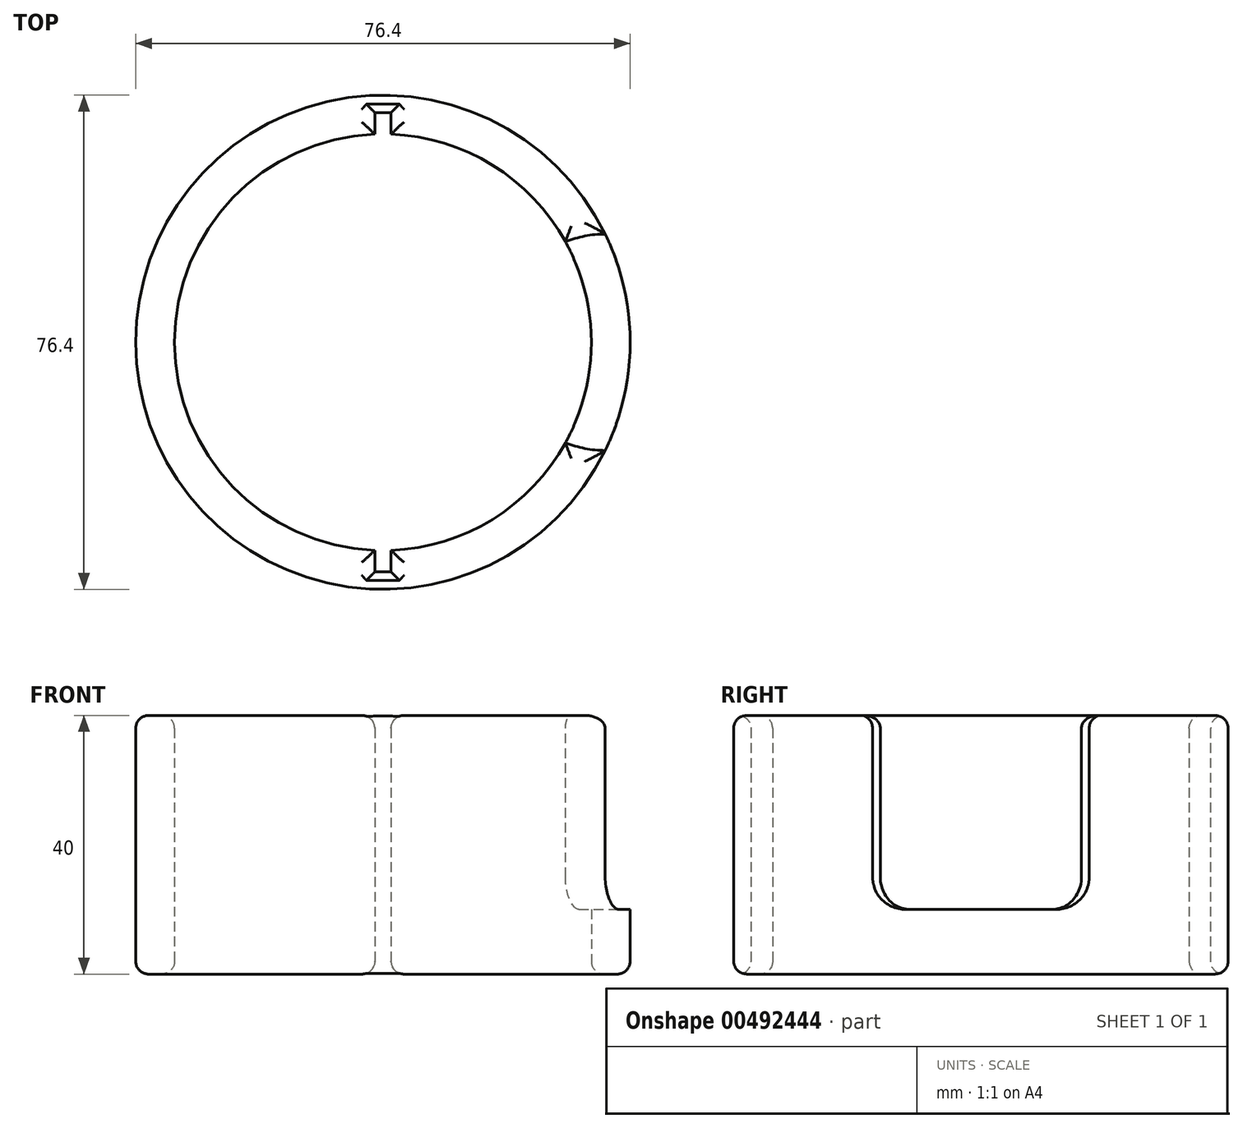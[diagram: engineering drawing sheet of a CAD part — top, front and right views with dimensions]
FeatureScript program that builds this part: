
annotation { "Feature Type Name" : "Feature", "Feature Type Description" : "" }
export const myFeature = defineFeature(function(context is Context, id is Id, definition is map)
    precondition{}
    {
        {
            var Q0;
            Q0=qCreatedBy(makeId("Top.planeOp"),FACE);
            var sketch = newSketch(context, id + "F0", { "sketchPlane" : qUnion([Q0])});
            skCircle(sketch, "E0", {"center": v(0, 0) * mm, "radius": 32.2 * mm});
            skCircle(sketch, "E1", {"center": v(0, 0) * mm, "radius": 38.2 * mm});
            skSolve(sketch);
        }
        {
            var Q0;
            Q0=makeQuery(id+"F0.imprint","IMPRINT",FACE,{"disambiguationData":[TD([[makeQuery(id+"F0.imprint","IMPRINT",EDGE,{"derivedFrom":sQuery(id+"F0.wireOp",EDGE,"E0")}),-1.0]])]});
            extrude(context, id + "F1", {"entities" : qUnion([Q0]), "depth" : 40 * mm});
        }
        {
            var Q0;
            Q0=makeQuery(id+"F1.opExtrude","CAP_FACE",FACE,{"disambiguationData":[OSD([sQuery(id+"F0.wireOp",EDGE,"E0"),sQuery(id+"F0.wireOp",EDGE,"E1")])],"isStart":false});
            var sketch = newSketch(context, id + "F2", { "sketchPlane" : qUnion([Q0])});
            skLineSegment(sketch, "E2.bottom", {"start": v(-1.25, 35.5) * mm, "end": v(1.25, 35.5) * mm});
            skLineSegment(sketch, "E2.top", {"start": v(-1.25, 31.5) * mm, "end": v(1.25, 31.5) * mm});
            skLineSegment(sketch, "E2.left", {"start": v(-1.25, 35.5) * mm, "end": v(-1.25, 31.5) * mm});
            skLineSegment(sketch, "E2.right", {"start": v(1.25, 35.5) * mm, "end": v(1.25, 31.5) * mm});
            skLineSegment(sketch, "E3.bottom", {"start": v(-1.25, -35.5) * mm, "end": v(1.25, -35.5) * mm});
            skLineSegment(sketch, "E3.top", {"start": v(-1.25, -31.5) * mm, "end": v(1.25, -31.5) * mm});
            skLineSegment(sketch, "E3.left", {"start": v(-1.25, -31.5) * mm, "end": v(-1.25, -35.5) * mm});
            skLineSegment(sketch, "E3.right", {"start": v(1.25, -31.5) * mm, "end": v(1.25, -35.5) * mm});
            skSolve(sketch);
        }
        {
            var Q0;
            {var subQ0=sQuery(id+"F2.wireOp",EDGE,"E3.bottom");Q0=makeQuery(id+"F2.imprint","IMPRINT",FACE,{"disambiguationData":[TD([[makeQuery(id+"F2.imprint","IMPRINT",EDGE,{"derivedFrom":subQ0}),1.0]])]});}
            var Q1;
            {var subQ0=sQuery(id+"F2.wireOp",EDGE,"E3.top");Q1=makeQuery(id+"F2.imprint","IMPRINT",FACE,{"disambiguationData":[TD([[makeQuery(id+"F2.imprint","IMPRINT",EDGE,{"derivedFrom":subQ0}),-1.0]])]});}
            var Q2;
            {var subQ0=sQuery(id+"F2.wireOp",EDGE,"E2.top");Q2=makeQuery(id+"F2.imprint","IMPRINT",FACE,{"disambiguationData":[TD([[makeQuery(id+"F2.imprint","IMPRINT",EDGE,{"derivedFrom":subQ0}),1.0]])]});}
            var Q3;
            {var subQ0=sQuery(id+"F2.wireOp",EDGE,"E2.bottom");Q3=makeQuery(id+"F2.imprint","IMPRINT",FACE,{"disambiguationData":[TD([[makeQuery(id+"F2.imprint","IMPRINT",EDGE,{"derivedFrom":subQ0}),-1.0]])]});}
            extrude(context, id + "F3", {"entities" : qUnion([Q0, Q1, Q2, Q3]), "operationType" : NewBodyOperationType.REMOVE, "endBound" : BoundingType.THROUGH_ALL, "oppositeDirection" : true, "depth" : 25 * mm});
        }
        {
            var Q0;
            Q0=makeQuery(id+"F1.opExtrude","CAP_FACE",FACE,{"disambiguationData":[OSD([sQuery(id+"F0.wireOp",EDGE,"E0"),sQuery(id+"F0.wireOp",EDGE,"E1")])],"isStart":false});
            var sketch = newSketch(context, id + "F4", { "sketchPlane" : qUnion([Q0])});
            skCircle(sketch, "E4", {"center": v(34.42, 0) * mm, "radius": 16.73 * mm});
            skSolve(sketch);
        }
        {
            var Q0;
            {var subQ0=sQuery(id+"F4.wireOp",EDGE,"E4");var subQ1=sQuery(id+"F0.wireOp",EDGE,"E1");var subQ2=makeQuery(id+"F1.opExtrude","CAP_EDGE",EDGE,{"disambiguationData":[OSD([subQ1])],"isStart":false});var subQ3=makeQuery(id+"F4.imprint","INTERSECT",VERTEX,{"disambiguationData":[OD(0.0)],"derivedFrom":[subQ2,subQ0]});Q0=makeQuery(id+"F4.imprint","IMPRINT",FACE,{"disambiguationData":[TD([[makeQuery(id+"F4.imprint","IMPRINT",EDGE,{"disambiguationData":[TD([[subQ3,1.0]])],"derivedFrom":subQ2}),1.0]])]});}
            extrude(context, id + "F5", {"entities" : qUnion([Q0]), "operationType" : NewBodyOperationType.REMOVE, "oppositeDirection" : true, "depth" : 30 * mm});
        }
        {
            var Q0;
            {var subQ0=sQuery(id+"F4.wireOp",EDGE,"E4");var subQ1=sQuery(id+"F0.wireOp",EDGE,"E1");Q0=makeQuery(id+"F5.boolean.opBoolean","COPY",EDGE,{"derivedFrom":makeQuery(id+"F5.opExtrude","CAP_EDGE",EDGE,{"disambiguationData":[OSD([subQ0]),TDD([makeQuery(id+"F4.imprint","IMPRINT",EDGE,{"disambiguationData":[TD([[makeQuery(id+"F4.imprint","INTERSECT",VERTEX,{"disambiguationData":[OD(0.0)],"derivedFrom":[makeQuery(id+"F1.opExtrude","CAP_EDGE",EDGE,{"disambiguationData":[OSD([subQ1])],"isStart":false}),subQ0]}),-1.0]])],"derivedFrom":subQ0})])],"isStart":false})});}
            var Q1;
            {var subQ0=sQuery(id+"F4.wireOp",EDGE,"E4");var subQ1=sQuery(id+"F0.wireOp",EDGE,"E1");Q1=makeQuery(id+"F5.boolean.opBoolean","COPY",EDGE,{"derivedFrom":makeQuery(id+"F5.opExtrude","CAP_EDGE",EDGE,{"disambiguationData":[OSD([subQ0]),TDD([makeQuery(id+"F4.imprint","IMPRINT",EDGE,{"disambiguationData":[TD([[makeQuery(id+"F4.imprint","INTERSECT",VERTEX,{"disambiguationData":[OD(1.0)],"derivedFrom":[makeQuery(id+"F1.opExtrude","CAP_EDGE",EDGE,{"disambiguationData":[OSD([subQ1])],"isStart":false}),subQ0]}),1.0]])],"derivedFrom":subQ0})])],"isStart":false})});}
            var Q2;
            {var subQ0=sQuery(id+"F4.wireOp",EDGE,"E4");var subQ1=sQuery(id+"F0.wireOp",EDGE,"E1");Q2=makeQuery(id+"F5.boolean.opBoolean","COPY",EDGE,{"derivedFrom":makeQuery(id+"F5.opExtrude","CAP_EDGE",EDGE,{"disambiguationData":[OSD([subQ0]),TDD([makeQuery(id+"F4.imprint","IMPRINT",EDGE,{"disambiguationData":[TD([[makeQuery(id+"F4.imprint","INTERSECT",VERTEX,{"disambiguationData":[OD(1.0)],"derivedFrom":[makeQuery(id+"F1.opExtrude","CAP_EDGE",EDGE,{"disambiguationData":[OSD([subQ1])],"isStart":false}),subQ0]}),1.0]])],"derivedFrom":subQ0})])],"isStart":true})});}
            var Q3;
            {var subQ0=sQuery(id+"F4.wireOp",EDGE,"E4");var subQ1=sQuery(id+"F0.wireOp",EDGE,"E1");Q3=makeQuery(id+"F5.boolean.opBoolean","COPY",EDGE,{"derivedFrom":makeQuery(id+"F5.opExtrude","CAP_EDGE",EDGE,{"disambiguationData":[OSD([subQ0]),TDD([makeQuery(id+"F4.imprint","IMPRINT",EDGE,{"disambiguationData":[TD([[makeQuery(id+"F4.imprint","INTERSECT",VERTEX,{"disambiguationData":[OD(0.0)],"derivedFrom":[makeQuery(id+"F1.opExtrude","CAP_EDGE",EDGE,{"disambiguationData":[OSD([subQ1])],"isStart":false}),subQ0]}),-1.0]])],"derivedFrom":subQ0})])],"isStart":true})});}
            fillet(context, id + "F6", {"entities" : qUnion([Q0, Q1, Q2, Q3]), "radius" : 5 * mm, "tangentPropagation" : true, "allowEdgeOverflow" : false});
        }
        {
            var Q0;
            Q0=makeQuery(id+"F1.opExtrude","CAP_FACE",FACE,{"disambiguationData":[OSD([sQuery(id+"F0.wireOp",EDGE,"E0"),sQuery(id+"F0.wireOp",EDGE,"E1")])],"isStart":false});
            var Q1;
            Q1=makeQuery(id+"F1.opExtrude","CAP_FACE",FACE,{"disambiguationData":[OSD([sQuery(id+"F0.wireOp",EDGE,"E0"),sQuery(id+"F0.wireOp",EDGE,"E1")])],"isStart":true});
            fillet(context, id + "F7", {"entities" : qUnion([Q0, Q1]), "radius" : 2 * mm, "tangentPropagation" : true, "allowEdgeOverflow" : false});
        }
    });
